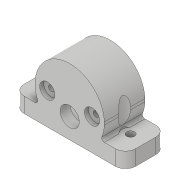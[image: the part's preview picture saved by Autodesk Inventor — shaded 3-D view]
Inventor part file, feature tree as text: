
AUTODESK INVENTOR PART (.ipt)
format: ipt  version: 2018 (Build 220112000, 112)  size: 379,392 bytes
history: native  units: in
note: dims shown in document units (in); Inventor stores cm internally (conversion verified against a paired STEP export)
features: sketch x16, extrude x13, projected_geometry x9, reference x5, fillet x4, other x4, plane x2, hole x2, mirror x1
ambient origin geometry x8: Origin, YZ Plane, XZ Plane, XY Plane, X Axis, Y Axis, Z Axis, Center Point
bodies: Solid1 (feature_tree)
feature tree (56):
  plane  "Work Plane1"
  extrude  "Extrusion1"  Depth=0.4in
  extrude  "Extrusion2"  Depth=1.25in
  extrude  "Extrusion3"  Depth=0.125in
  extrude  "Extrusion4"  Depth=0.1in
  fillet  "Fillet1"  Radius=0.375in
  fillet  "Fillet2"  Radius=0.75in
  extrude  "Extrusion5"  Depth=0.0625in
  sketch  "Sketch7"  dims[d16=0.25in d17=0.1in d18=0.0in]
  extrude  "Extrusion6"  Depth=0.1in TaperAngle=0.0deg
  extrude  "Extrusion8"  Depth=4.0in TaperAngle=0.0deg
  extrude  "Extrusion9"  TaperAngle=0.0deg  [1 undecoded]
  extrude  "Extrusion11"  Depth=0.125in
  extrude  "Extrusion12"  Depth=4.0in TaperAngle=0.0deg
  hole  "Hole3"  [1 undecoded]
  extrude  "Extrusion13"  Depth=0.1in TaperAngle=0.0deg
  extrude  "Extrusion14"  Depth=0.1in TaperAngle=0.0deg
  fillet  "Fillet4"  Radius=0.0625in
  plane  "Work Plane2"
  mirror  "Mirror1"
  fillet  "Fillet5"  Radius=0.25in
  hole  "Hole4"  [1 undecoded]
  extrude  "Extrusion15"  Depth=2.0in
  sketch  "Sketch2"  dims[d0=0.025in d1=0.4in]
  reference  "Reference1"
  reference  "Reference2"
  sketch  "Sketch3"  dims[d2=1.25in d3=1.25in]
  sketch  "Sketch4"  dims[d4=0.25in d5=0.125in]
  projected_geometry  "Projected Loop1"
  projected_geometry  "Projected Loop2"
  sketch  "Sketch5"  dims[d6=0.25in d7=0.0in d8=0.1in d9=0.375in d10=0.0in d11=0.75in d12=0.0in]
  projected_geometry  "Projected Loop3"
  sketch  "Sketch6"  dims[d13=0.75in d14=0.0in d15=0.0625in]
  projected_geometry  "Projected Loop4"
  projected_geometry  "Projected Loop5"
  sketch  "Sketch8"  dims[d20=0.1in d21=0.0in d24=4.0in d25=0.0in]
  projected_geometry  "Projected Loop6"
  sketch  "Sketch10"  dims[d26=4.0in d27=0.0in d41=0.0in]
  sketch  "Sketch12"  dims[d42=0.0in d43=0.125in]
  projected_geometry  "Projected Loop7"
  sketch  "Sketch15"  dims[d44=0.125in d45=4.0in d46=0.0in]
  sketch  "Sketch17"  dims[d59=4.0in d60=0.0in]
  sketch  "Sketch18"  dims[d61=0.142in d62=0.75in d63=0.248in d64=0.25in d65=90.0deg d66=1.0in d67=0.8108in d68=0.375in]
  reference  "Reference4"
  reference  "Reference5"
  reference  "Reference6"
  sketch  "Sketch19"  dims[d69=0.375in d70=0.1in d71=0.0in]
  sketch  "Sketch21"  dims[d76=0.375in d77=0.1in d78=0.0in d79=0.0625in d80=0.25in]
  sketch  "Sketch22"  dims[d81=0.5in d82=0.5in]
  sketch  "Sketch23"  dims[d83=0.375in d84=2.0in d85=0.375in d86=0.194in d87=0.75in d88=0.332in d89=0.25in d90=0.5635in d91=1.0in d92=0.8108in d93=1.0in d94=0.0in]
  projected_geometry  "Projected Loop10"
  projected_geometry  "Projected Loop11"
  parser-record x1  (decoder bookkeeping rows leaked as tree rows — omitted from the tree; the rows remain in map.json)
  other  "Motor.iam"
  other  "39530_txm-dc gearhead motor:1"
  other  "Assembly2"
note: 3 required parameter values undecoded (feature->parameter linkage not recoverable at this tier; creation-order binding heuristic only, values carry confidence <= 0.55)
note: 1 file-system path scrubbed to <path> (originals preserved in map.json)
